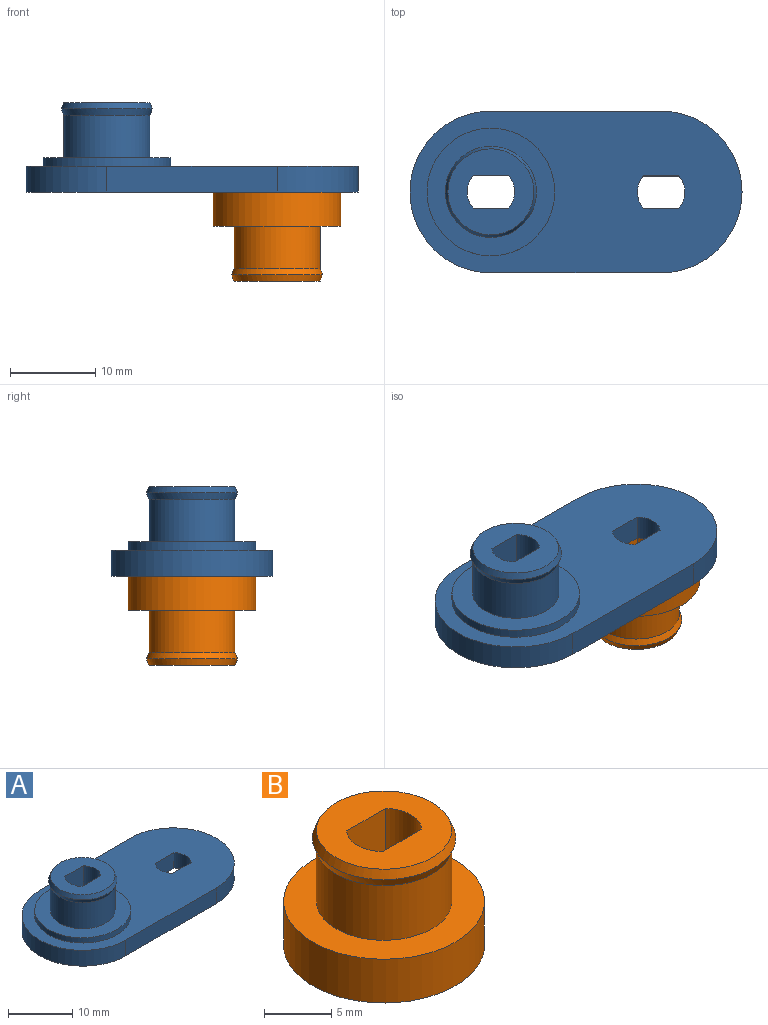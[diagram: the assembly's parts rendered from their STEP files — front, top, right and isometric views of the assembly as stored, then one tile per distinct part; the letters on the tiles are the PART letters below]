
ASSEMBLY  parts=2 mates=1
PART A: 20 faces, bbox 39x19x10.5 mm
  f0: plane 20x3mm, normal (0,1,0), area 60mm2, adj f1,f3,f4,f5
  f1: cylinder r=9.5mm len=19mm, axis (0,0,-1), area 89.5mm2, adj f0,f2,f4,f5
  f2: plane 20x3mm, normal (0,-1,0), area 60mm2, adj f1,f3,f4,f5
  f3: cylinder r=9.5mm len=19mm, axis (0,0,-1), area 89.5mm2, adj f0,f2,f4,f5
  f4: plane 39x19mm, normal (0,0,1), area 467.3mm2, adj f0,f1,f2,f3,f11,f16,f17,f18
  f5: plane 39x19mm, normal (0,0,-1), area 624.5mm2, adj f0,f1,f2,f3,f7,f8,f9,f10
  f6: cylinder r=5.05mm len=10.1mm, axis (0,0,-1), area 158.7mm2, adj f12,f14
  f7: cylinder r=2.8mm len=10.5mm, axis (0,0,-1), area 43.9mm2, adj f5,f8,f10,f13
  f8: plane 10.5x4.11mm, normal (0,-1,0), area 43.2mm2, adj f5,f7,f9,f13
  f9: cylinder r=2.8mm len=10.5mm, axis (0,0,-1), area 43.9mm2, adj f5,f8,f10,f13
  f10: plane 10.5x4.11mm, normal (0,1,0), area 43.2mm2, adj f5,f7,f9,f13
  f11: cylinder r=7.5mm len=15mm, axis (0,0,-1), area 47.1mm2, adj f4,f12
  f12: plane 15x15mm, normal (0,0,1), area 96.6mm2, adj f6,f11
  f13: plane 10.1x10.1mm, normal (0,0,1), area 60.6mm2, adj f7,f8,f9,f10,f15
  f14: cone r=5.35mm half-angle=21.8deg, axis (0,0,1), area 26.4mm2, adj f6,f15
  f15: cone r=5.05mm half-angle=21.8deg, axis (0,0,-1), area 26.4mm2, adj f13,f14
  f16: plane 4.11x3mm, normal (0,-1,0), area 12.3mm2, adj f4,f5,f17,f19
  f17: cylinder r=2.8mm len=3.8mm, axis (0,0,-1), area 12.5mm2, adj f4,f5,f16,f18
  f18: plane 4.11x3mm, normal (0,1,0), area 12.3mm2, adj f4,f5,f17,f19
  f19: cylinder r=2.8mm len=3.8mm, axis (0,0,-1), area 12.5mm2, adj f4,f5,f16,f18
PART B: 11 faces, bbox 15x15x10.5 mm
  f0: plane 15x15mm, normal (0,0,1), area 96.6mm2, adj f4,f7
  f1: cylinder r=2.8mm len=10.5mm, axis (0,0,-1), area 43.9mm2, adj f2,f5,f6,f8
  f2: plane 10.5x4.11mm, normal (0,-1,0), area 43.2mm2, adj f1,f3,f6,f8
  f3: cylinder r=2.8mm len=10.5mm, axis (0,0,-1), area 43.9mm2, adj f2,f5,f6,f8
  f4: cylinder r=7.5mm len=15mm, axis (0,0,-1), area 188.5mm2, adj f0,f6
  f5: plane 10.5x4.11mm, normal (0,1,0), area 43.2mm2, adj f1,f3,f6,f8
  f6: plane 15x15mm, normal (0,0,-1), area 157.2mm2, adj f1,f2,f3,f4,f5
  f7: cylinder r=5.05mm len=10.1mm, axis (0,0,-1), area 158.7mm2, adj f0,f9
  f8: plane 10.1x10.1mm, normal (0,0,1), area 60.6mm2, adj f1,f2,f3,f5,f10
  f9: cone r=5.35mm half-angle=21.8deg, axis (0,0,1), area 26.4mm2, adj f7,f10
  f10: cone r=5.05mm half-angle=21.8deg, axis (0,0,-1), area 26.4mm2, adj f8,f9
PLACE A t=(-9.17,-29.24,0.63)mm
PLACE B rot(axis=(1,0,0),180deg) t=(10.83,-9.24,0.63)mm
MATE fastened A.f3 <-> B.f4  axis (0,0,-1) through (10.83,-9.24,0.63)mm
